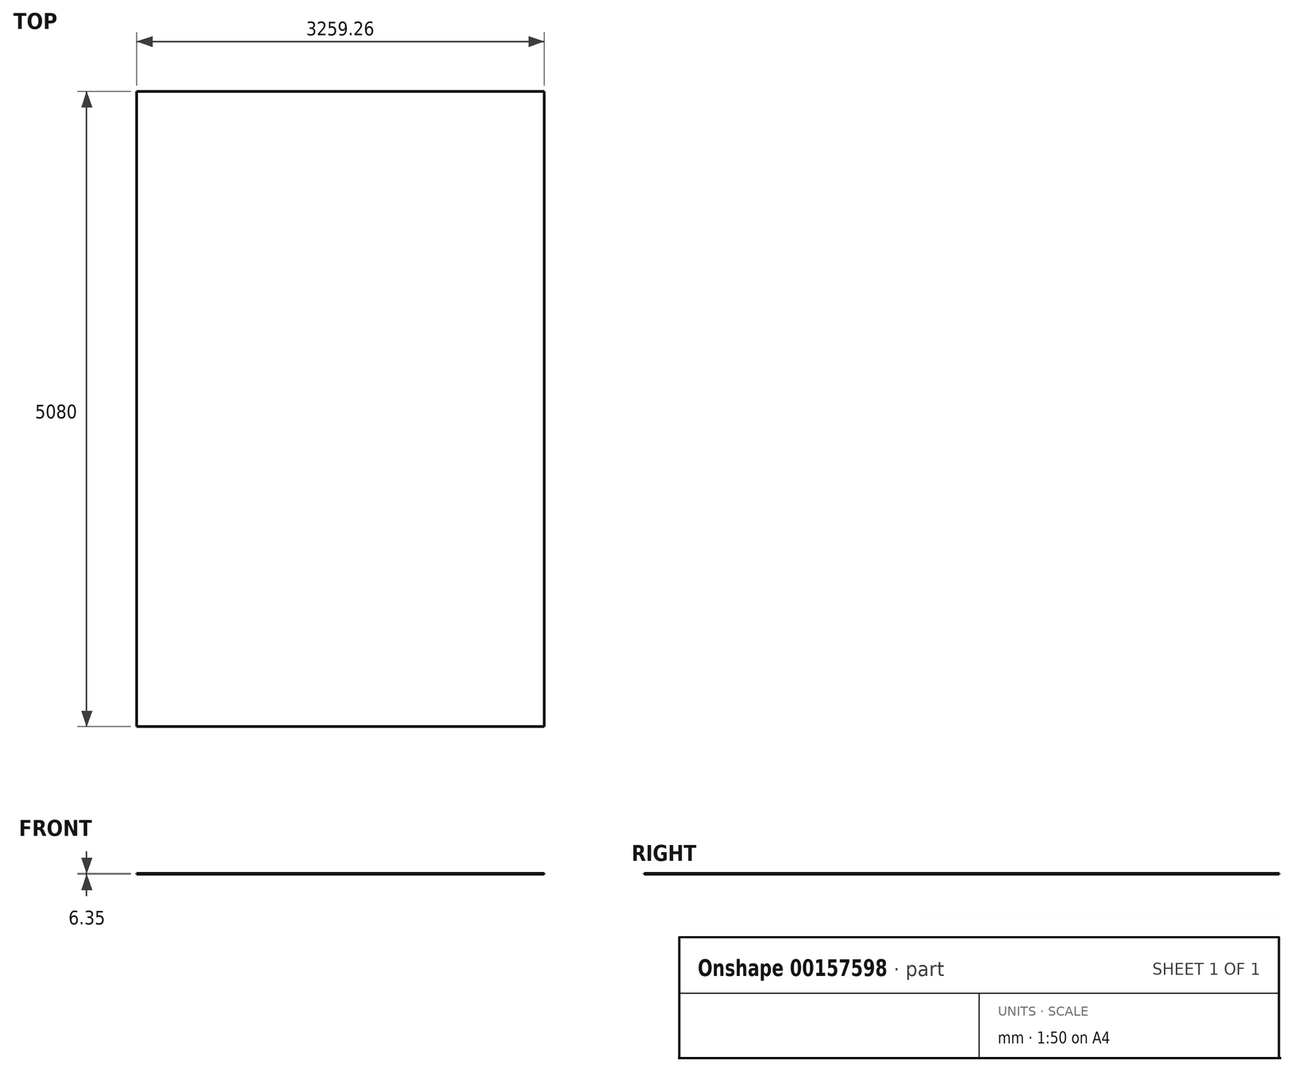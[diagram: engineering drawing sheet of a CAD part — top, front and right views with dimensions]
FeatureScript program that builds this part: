
annotation { "Feature Type Name" : "Feature", "Feature Type Description" : "" }
export const myFeature = defineFeature(function(context is Context, id is Id, definition is map)
    precondition{}
    {
        {
            var Q0;
            Q0=qCreatedBy(makeId("Top.planeOp"),FACE);
            var sketch = newSketch(context, id + "F0", { "sketchPlane" : qUnion([Q0])});
            skLineSegment(sketch, "E0.bottom", {"start": v(1629.63, 2540) * mm, "end": v(-1629.63, 2540) * mm});
            skLineSegment(sketch, "E0.top", {"start": v(1629.63, -2540) * mm, "end": v(-1629.63, -2540) * mm});
            skLineSegment(sketch, "E0.left", {"start": v(1629.63, 2540) * mm, "end": v(1629.63, -2540) * mm});
            skLineSegment(sketch, "E0.right", {"start": v(-1629.63, 2540) * mm, "end": v(-1629.63, -2540) * mm});
            skPoint(sketch, "E0.middle", {"position": v(0, 0) * mm});
            skSolve(sketch);
        }
        {
            var Q0;
            Q0=makeQuery(id+"F0.imprint","IMPRINT",FACE,{"disambiguationData":[TD([[makeQuery(id+"F0.imprint","IMPRINT",EDGE,{"derivedFrom":sQuery(id+"F0.wireOp",EDGE,"E0.bottom")}),1.0]])]});
            extrude(context, id + "F1", {"entities" : qUnion([Q0]), "depth" : 6.35 * mm});
        }
    });
